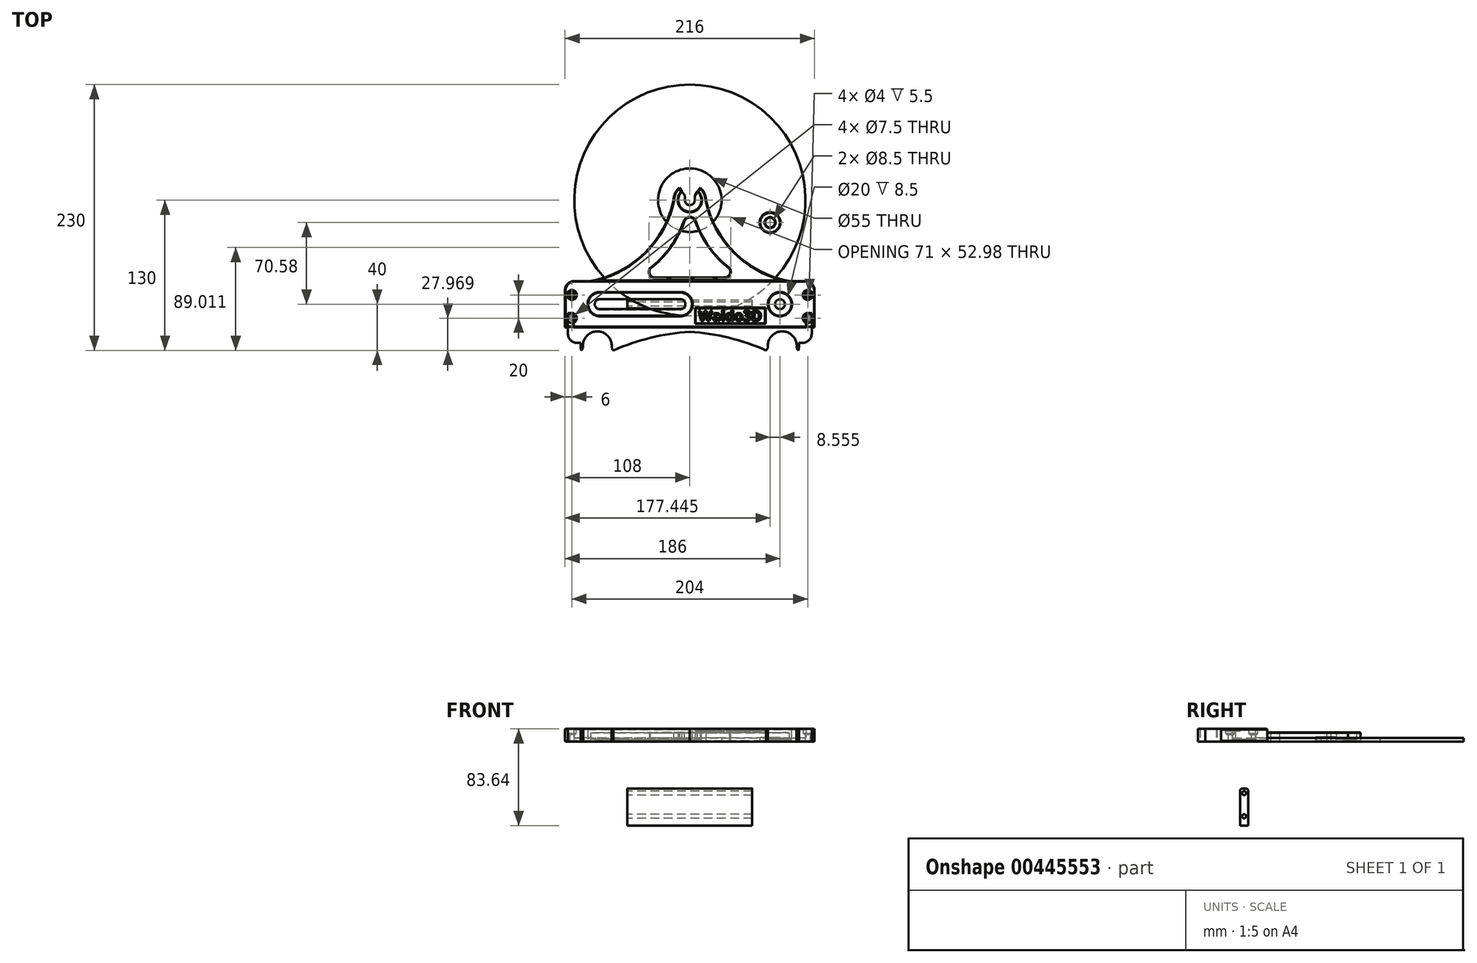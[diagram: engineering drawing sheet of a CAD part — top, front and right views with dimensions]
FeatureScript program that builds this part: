
annotation { "Feature Type Name" : "Feature", "Feature Type Description" : "" }
export const myFeature = defineFeature(function(context is Context, id is Id, definition is map)
    precondition{}
    {
        {
            var Q0;
            Q0=qCreatedBy(makeId("Top.planeOp"),FACE);
            var sketch = newSketch(context, id + "F0", { "sketchPlane" : qUnion([Q0])});
            skLineSegment(sketch, "E0", {"start": v(0, 0) * mm, "end": v(0, 90) * mm});
            skCircle(sketch, "E1", {"center": v(0, 90) * mm, "radius": 100 * mm});
            skCircle(sketch, "E2", {"center": v(0, 90) * mm, "radius": 27.5 * mm});
            skSolve(sketch);
        }
        {
            var Q0;
            Q0 = qSketchRegion(id + "F0", true);
            extrude(context, id + "F1", {"entities" : qUnion([Q0]), "depth" : 3 * mm});
        }
        {
            var Q0;
            Q0=qCreatedBy(makeId("Top.planeOp"),FACE);
            var sketch = newSketch(context, id + "F2", { "sketchPlane" : qUnion([Q0])});
            skLineSegment(sketch, "E3.top", {"start": v(100, 20.03) * mm, "end": v(-100, 20.03) * mm});
            skPoint(sketch, "E3.middle", {"position": v(0, 0) * mm});
            skArc(sketch, "E4", {"start": v(108, 12.03) * mm, "mid": v(105.66, 17.69) * mm, "end": v(100, 20.03) * mm});
            skPoint(sketch, "E5.orphan", {"position": v(108, 20.03) * mm});
            skArc(sketch, "E6.MirrorCS", {"start": v(-108, 12.03) * mm, "mid": v(-105.66, 17.69) * mm, "end": v(-100, 20.03) * mm});
            skPoint(sketch, "E7.orphan", {"position": v(-108, 20.03) * mm});
            skCircle(sketch, "E8", {"center": v(-78, 0) * mm, "radius": 4.25 * mm});
            skCircle(sketch, "E9", {"center": v(-8, 0) * mm, "radius": 4.25 * mm});
            skCircle(sketch, "E10", {"center": v(78, 0) * mm, "radius": 4.25 * mm});
            skLineSegment(sketch, "E11", {"start": v(-78, 4.25) * mm, "end": v(-8, 4.25) * mm});
            skLineSegment(sketch, "E12", {"start": v(-8.4, -4.23) * mm, "end": v(-77.6, -4.23) * mm});
            skPoint(sketch, "E13.orphan", {"position": v(108, -20.03) * mm});
            skPoint(sketch, "E14.orphan", {"position": v(-108, -20.03) * mm});
            skLineSegment(sketch, "E15", {"start": v(108, 12.03) * mm, "end": v(108, -20.03) * mm});
            skLineSegment(sketch, "E16", {"start": v(-108, -20.03) * mm, "end": v(-108, 12.03) * mm});
            skLineSegment(sketch, "E17", {"start": v(-108, -20.03) * mm, "end": v(108, -20.03) * mm});
            skCircle(sketch, "E18", {"center": v(102, 7.97) * mm, "radius": 2 * mm});
            skCircle(sketch, "E19", {"center": v(102, -12.03) * mm, "radius": 2 * mm});
            skCircle(sketch, "E20.MirrorC", {"center": v(-102, 7.97) * mm, "radius": 2 * mm});
            skCircle(sketch, "E21.MirrorC", {"center": v(-102, -12.03) * mm, "radius": 2 * mm});
            skSolve(sketch);
        }
        {
            var Q0;
            Q0 = qSketchRegion(id + "F2", true);
            extrude(context, id + "F3", {"entities" : qUnion([Q0]), "depth" : 11 * mm});
        }
        {
            var Q0;
            {var subQ0=sQuery(id+"F2.wireOp",EDGE,"E21.MirrorC");var subQ1=sQuery(id+"F2.wireOp",EDGE,"E20.MirrorC");var subQ2=sQuery(id+"F2.wireOp",EDGE,"E19");var subQ3=sQuery(id+"F2.wireOp",EDGE,"E18");var subQ4=sQuery(id+"F2.wireOp",EDGE,"E17");var subQ5=sQuery(id+"F2.wireOp",EDGE,"E6.MirrorCS");var subQ6=sQuery(id+"F2.wireOp",EDGE,"E4");var subQ7=sQuery(id+"F2.wireOp",EDGE,"E8");var subQ8=sQuery(id+"F2.wireOp",EDGE,"E3.top");var subQ9=sQuery(id+"F2.wireOp",EDGE,"E16");var subQ10=sQuery(id+"F2.wireOp",EDGE,"E9");var subQ11=sQuery(id+"F2.wireOp",EDGE,"E10");var subQ12=sQuery(id+"F2.wireOp",EDGE,"E11");var subQ13=sQuery(id+"F2.wireOp",EDGE,"E12");var subQ14=sQuery(id+"F2.wireOp",EDGE,"E15");Q0=makeQuery(id+"F7.boolean.opBoolean","SPLIT",FACE,{"disambiguationData":[TD([makeQuery(id+"F3.opExtrude","SWEPT_FACE",FACE,{"disambiguationData":[OSD([subQ8])]})])],"derivedFrom":makeQuery(id+"F3.opExtrude","CAP_FACE",FACE,{"disambiguationData":[OSD([subQ8,subQ6,subQ5,subQ7,subQ10,subQ11,subQ12,subQ13,subQ14,subQ9,subQ4,subQ3,subQ2,subQ1,subQ0])],"isStart":false})});}
            var sketch = newSketch(context, id + "F4", { "sketchPlane" : qUnion([Q0])});
            skLineSegment(sketch, "E22.bottom", {"start": v(65, -16.53) * mm, "end": v(5, -16.53) * mm});
            skLineSegment(sketch, "E22.top", {"start": v(65, -3.53) * mm, "end": v(5, -3.53) * mm});
            skLineSegment(sketch, "E22.left", {"start": v(65, -16.53) * mm, "end": v(65, -3.53) * mm});
            skLineSegment(sketch, "E22.right", {"start": v(5, -16.53) * mm, "end": v(5, -3.53) * mm});
            skPoint(sketch, "E22.middle", {"position": v(35, -10.03) * mm});
            skSolve(sketch);
        }
        {
            var Q0;
            Q0 = qSketchRegion(id + "F4", true);
            extrude(context, id + "F5", {"entities" : qUnion([Q0]), "operationType" : NewBodyOperationType.REMOVE, "oppositeDirection" : true, "depth" : 2 * mm});
        }
        {
            var Q0;
            Q0=makeQuery(id+"F5.boolean.opBoolean","COPY",FACE,{"derivedFrom":makeQuery(id+"F5.opExtrude","CAP_FACE",FACE,{"disambiguationData":[OSD([sQuery(id+"F4.wireOp",EDGE,"E22.bottom"),sQuery(id+"F4.wireOp",EDGE,"E22.top"),sQuery(id+"F4.wireOp",EDGE,"E22.left"),sQuery(id+"F4.wireOp",EDGE,"E22.right")])],"isStart":false})});
            var sketch = newSketch(context, id + "F6", { "sketchPlane" : qUnion([Q0])});
            skText(sketch, "E23", { "text": "Waldo3D", "fontName": "OpenSans-Bold.ttf"});
            skPoint(sketch, "E24.middle", {"position": v(35, -10.03) * mm});
            const initialGuessF6  = {"E23": [0.0075, -0.01448, 1, 0, 0.0089]};
            skSetInitialGuess(sketch, initialGuessF6);
            skSolve(sketch);
        }
        {
            var Q0;
            Q0 = qSketchRegion(id + "F6", true);
            extrude(context, id + "F7", {"entities" : qUnion([Q0]), "operationType" : NewBodyOperationType.ADD, "depth" : 2 * mm});
        }
        {
            var Q0;
            Q0=makeQuery(id+"F3.opExtrude","CAP_FACE",FACE,{"disambiguationData":[OSD([sQuery(id+"F2.wireOp",EDGE,"E3.bottom"),sQuery(id+"F2.wireOp",EDGE,"E3.top"),sQuery(id+"F2.wireOp",EDGE,"E3.left"),sQuery(id+"F2.wireOp",EDGE,"E3.right"),sQuery(id+"F2.wireOp",EDGE,"E4"),sQuery(id+"F2.wireOp",EDGE,"E6.MirrorCS"),sQuery(id+"F2.wireOp",EDGE,"E8"),sQuery(id+"F2.wireOp",EDGE,"E9"),sQuery(id+"F2.wireOp",EDGE,"E10"),sQuery(id+"F2.wireOp",EDGE,"E11"),sQuery(id+"F2.wireOp",EDGE,"E12")])],"isStart":false});
            var sketch = newSketch(context, id + "F8", { "sketchPlane" : qUnion([Q0])});
            skCircle(sketch, "E25", {"center": v(-78, 0) * mm, "radius": 10 * mm});
            skCircle(sketch, "E26", {"center": v(-8, 0) * mm, "radius": 10 * mm});
            skLineSegment(sketch, "E27", {"start": v(-78, 10) * mm, "end": v(-8, 10) * mm});
            skLineSegment(sketch, "E28", {"start": v(-8, -10) * mm, "end": v(-78, -10) * mm});
            skCircle(sketch, "E29", {"center": v(78, 0) * mm, "radius": 10 * mm});
            skSolve(sketch);
        }
        {
            var Q0;
            Q0 = qSketchRegion(id + "F8", true);
            extrude(context, id + "F9", {"entities" : qUnion([Q0]), "operationType" : NewBodyOperationType.REMOVE, "oppositeDirection" : true, "depth" : 9 * mm});
        }
        {
            var Q0;
            Q0=makeQuery(id+"F3.opExtrude","CAP_FACE",FACE,{"disambiguationData":[OSD([sQuery(id+"F2.wireOp",EDGE,"E3.bottom"),sQuery(id+"F2.wireOp",EDGE,"E3.top"),sQuery(id+"F2.wireOp",EDGE,"E3.left"),sQuery(id+"F2.wireOp",EDGE,"E3.right"),sQuery(id+"F2.wireOp",EDGE,"E4"),sQuery(id+"F2.wireOp",EDGE,"E6.MirrorCS"),sQuery(id+"F2.wireOp",EDGE,"E8"),sQuery(id+"F2.wireOp",EDGE,"E9"),sQuery(id+"F2.wireOp",EDGE,"E10"),sQuery(id+"F2.wireOp",EDGE,"E11"),sQuery(id+"F2.wireOp",EDGE,"E12")])],"isStart":false});
            var sketch = newSketch(context, id + "F10", { "sketchPlane" : qUnion([Q0])});
            skCircle(sketch, "E30", {"center": v(102, 7.97) * mm, "radius": 3.75 * mm});
            skCircle(sketch, "E31", {"center": v(102, -12.03) * mm, "radius": 3.75 * mm});
            skCircle(sketch, "E32.MirrorC", {"center": v(-102, 7.97) * mm, "radius": 3.75 * mm});
            skCircle(sketch, "E33.MirrorC", {"center": v(-102, -12.03) * mm, "radius": 3.75 * mm});
            skSolve(sketch);
        }
        {
            var Q0;
            Q0 = qSketchRegion(id + "F10", true);
            extrude(context, id + "F11", {"entities" : qUnion([Q0]), "operationType" : NewBodyOperationType.REMOVE, "oppositeDirection" : true, "depth" : 5 * mm});
        }
        {
            var Q0;
            Q0=makeQuery(id+"F11.boolean.opBoolean","COPY",EDGE,{"derivedFrom":makeQuery(id+"F11.opExtrude","CAP_EDGE",EDGE,{"disambiguationData":[OSD([sQuery(id+"F10.wireOp",EDGE,"E32.MirrorC")])],"isStart":false})});
            var Q1;
            Q1=makeQuery(id+"F11.boolean.opBoolean","COPY",EDGE,{"derivedFrom":makeQuery(id+"F11.opExtrude","CAP_EDGE",EDGE,{"disambiguationData":[OSD([sQuery(id+"F10.wireOp",EDGE,"E33.MirrorC")])],"isStart":false})});
            var Q2;
            Q2=makeQuery(id+"F11.boolean.opBoolean","COPY",EDGE,{"derivedFrom":makeQuery(id+"F11.opExtrude","CAP_EDGE",EDGE,{"disambiguationData":[OSD([sQuery(id+"F10.wireOp",EDGE,"E30")])],"isStart":false})});
            var Q3;
            Q3=makeQuery(id+"F11.boolean.opBoolean","COPY",EDGE,{"derivedFrom":makeQuery(id+"F11.opExtrude","CAP_EDGE",EDGE,{"disambiguationData":[OSD([sQuery(id+"F10.wireOp",EDGE,"E31")])],"isStart":false})});
            chamfer(context, id + "F12", {"entities" : qUnion([Q0, Q1, Q2, Q3]), "width" : 1 * mm, "tangentPropagation" : true});
        }
        {
            var Q0;
            Q0=qCreatedBy(makeId("Top.planeOp"),FACE);
            var sketch = newSketch(context, id + "F13", { "sketchPlane" : qUnion([Q0])});
            skLineSegment(sketch, "E34", {"start": v(0, 20) * mm, "end": v(86.03, 20) * mm});
            skLineSegment(sketch, "E35", {"start": v(0, 20) * mm, "end": v(0, 90) * mm});
            skArc(sketch, "E36", {"start": v(-8.97, 100.75) * mm, "mid": v(-12.68, 95.93) * mm, "end": v(-14, 90) * mm});
            skArc(sketch, "E37", {"start": v(-4.25, 90) * mm, "mid": v(0, 85.75) * mm, "end": v(4.25, 90) * mm});
            skLineSegment(sketch, "E38", {"start": v(4.25, 90) * mm, "end": v(4.25, 94) * mm});
            skLineSegment(sketch, "E39", {"start": v(4.25, 94) * mm, "end": v(8.97, 100.75) * mm});
            skLineSegment(sketch, "E40.MirrorCS", {"start": v(-4.25, 90) * mm, "end": v(-4.25, 94) * mm});
            skLineSegment(sketch, "E41.MirrorCS", {"start": v(-4.25, 94) * mm, "end": v(-8.97, 100.75) * mm});
            skArc(sketch, "E42", {"start": v(14, 90) * mm, "mid": v(39.34, 44.02) * mm, "end": v(86.03, 20) * mm});
            skArc(sketch, "E43.MirrorCS", {"start": v(-14, 90) * mm, "mid": v(-39.34, 44.02) * mm, "end": v(-86.03, 20) * mm});
            skLineSegment(sketch, "E44.MirrorCS", {"start": v(0, 20) * mm, "end": v(-86.03, 20) * mm});
            skArc(sketch, "E45", {"start": v(30, 23.02) * mm, "mid": v(34.34, 25.54) * mm, "end": v(34.32, 30.55) * mm});
            skArc(sketch, "E46.trimOffspring", {"start": v(14, 90) * mm, "mid": v(12.68, 95.93) * mm, "end": v(8.97, 100.75) * mm});
            skLineSegment(sketch, "E47", {"start": v(30, 23.02) * mm, "end": v(0, 23.02) * mm});
            skArc(sketch, "E48.MirrorC", {"start": v(-30, 23.02) * mm, "mid": v(-34.6, 26.06) * mm, "end": v(-33.61, 31.48) * mm});
            skLineSegment(sketch, "E49.MirrorCS", {"start": v(-30, 23.02) * mm, "end": v(0, 23.02) * mm});
            skCircle(sketch, "E50", {"center": v(0, 70) * mm, "radius": 5 * mm});
            skArc(sketch, "E51", {"start": v(4.77, 71.5) * mm, "mid": v(16.61, 48.9) * mm, "end": v(34.32, 30.55) * mm});
            skArc(sketch, "E52.MirrorCS", {"start": v(-4.77, 71.5) * mm, "mid": v(-16.61, 48.9) * mm, "end": v(-34.32, 30.55) * mm});
            skSolve(sketch);
        }
        {
            var Q0;
            Q0 = qSketchRegion(id + "F13", true);
            extrude(context, id + "F14", {"entities" : qUnion([Q0]), "depth" : 8 * mm});
        }
        {
            var Q0;
            Q0=makeQuery(id+"F14.opExtrude","CAP_FACE",FACE,{"disambiguationData":[OSD([sQuery(id+"F13.wireOp",EDGE,"E34"),sQuery(id+"F13.wireOp",EDGE,"E36"),sQuery(id+"F13.wireOp",EDGE,"E37"),sQuery(id+"F13.wireOp",EDGE,"E38"),sQuery(id+"F13.wireOp",EDGE,"E39"),sQuery(id+"F13.wireOp",EDGE,"E40.MirrorCS"),sQuery(id+"F13.wireOp",EDGE,"E41.MirrorCS"),sQuery(id+"F13.wireOp",EDGE,"E42"),sQuery(id+"F13.wireOp",EDGE,"E43.MirrorCS"),sQuery(id+"F13.wireOp",EDGE,"E44.MirrorCS"),sQuery(id+"F13.wireOp",EDGE,"klo4OWiA-xBeZ-rQVl-mnmB-Yb4P8nKjesbg"),sQuery(id+"F13.wireOp",EDGE,"E45"),sQuery(id+"F13.wireOp",EDGE,"E46.trimOffspring"),sQuery(id+"F13.wireOp",EDGE,"pojwg80n-vTzl-4vHL-MMqQ-xkOF31NqBd4l"),sQuery(id+"F13.wireOp",EDGE,"E47"),sQuery(id+"F13.wireOp",EDGE,"45ded926-9557-4482-96ae-ffeaec27a78e0.MirrorCS"),sQuery(id+"F13.wireOp",EDGE,"E48.MirrorC"),sQuery(id+"F13.wireOp",EDGE,"E49.MirrorCS")])],"isStart":false});
            var sketch = newSketch(context, id + "F15", { "sketchPlane" : qUnion([Q0])});
            skCircle(sketch, "E53", {"center": v(0, 90) * mm, "radius": 10 * mm});
            skSolve(sketch);
        }
        {
            var Q0;
            Q0 = qSketchRegion(id + "F15", true);
            extrude(context, id + "F16", {"entities" : qUnion([Q0]), "operationType" : NewBodyOperationType.REMOVE, "oppositeDirection" : true, "depth" : 6 * mm});
        }
        {
            var Q0;
            Q0=makeQuery(id+"F3.opExtrude","CAP_FACE",FACE,{"disambiguationData":[OSD([sQuery(id+"F2.wireOp",EDGE,"E3.top"),sQuery(id+"F2.wireOp",EDGE,"E4"),sQuery(id+"F2.wireOp",EDGE,"E6.MirrorCS"),sQuery(id+"F2.wireOp",EDGE,"E8"),sQuery(id+"F2.wireOp",EDGE,"E9"),sQuery(id+"F2.wireOp",EDGE,"E10"),sQuery(id+"F2.wireOp",EDGE,"E11"),sQuery(id+"F2.wireOp",EDGE,"E12"),sQuery(id+"F2.wireOp",EDGE,"E15"),sQuery(id+"F2.wireOp",EDGE,"E16"),sQuery(id+"F2.wireOp",EDGE,"E17"),sQuery(id+"F2.wireOp",EDGE,"E18"),sQuery(id+"F2.wireOp",EDGE,"E19"),sQuery(id+"F2.wireOp",EDGE,"E20.MirrorC"),sQuery(id+"F2.wireOp",EDGE,"E21.MirrorC")])],"isStart":false});
            var Q1;
            Q1=makeQuery(id+"F14.opExtrude","CAP_FACE",FACE,{"disambiguationData":[OSD([sQuery(id+"F13.wireOp",EDGE,"E34"),sQuery(id+"F13.wireOp",EDGE,"E36"),sQuery(id+"F13.wireOp",EDGE,"E37"),sQuery(id+"F13.wireOp",EDGE,"E38"),sQuery(id+"F13.wireOp",EDGE,"E39"),sQuery(id+"F13.wireOp",EDGE,"E40.MirrorCS"),sQuery(id+"F13.wireOp",EDGE,"E41.MirrorCS"),sQuery(id+"F13.wireOp",EDGE,"E42"),sQuery(id+"F13.wireOp",EDGE,"E43.MirrorCS"),sQuery(id+"F13.wireOp",EDGE,"E44.MirrorCS"),sQuery(id+"F13.wireOp",EDGE,"E45"),sQuery(id+"F13.wireOp",EDGE,"E46.trimOffspring"),sQuery(id+"F13.wireOp",EDGE,"E47"),sQuery(id+"F13.wireOp",EDGE,"E48.MirrorC"),sQuery(id+"F13.wireOp",EDGE,"E49.MirrorCS"),sQuery(id+"F13.wireOp",EDGE,"E50"),sQuery(id+"F13.wireOp",EDGE,"E51"),sQuery(id+"F13.wireOp",EDGE,"E52.MirrorCS")])],"isStart":false});
            var Q2;
            Q2=makeQuery(id+"F21.opBoolean","MERGE",FACE,{"derivedFrom":[makeQuery(id+"F3.opExtrude","CAP_FACE",FACE,{"disambiguationData":[OSD([sQuery(id+"F2.wireOp",EDGE,"E3.top"),sQuery(id+"F2.wireOp",EDGE,"E4"),sQuery(id+"F2.wireOp",EDGE,"E6.MirrorCS"),sQuery(id+"F2.wireOp",EDGE,"E8"),sQuery(id+"F2.wireOp",EDGE,"E9"),sQuery(id+"F2.wireOp",EDGE,"E10"),sQuery(id+"F2.wireOp",EDGE,"E11"),sQuery(id+"F2.wireOp",EDGE,"E12"),sQuery(id+"F2.wireOp",EDGE,"E15"),sQuery(id+"F2.wireOp",EDGE,"E16"),sQuery(id+"F2.wireOp",EDGE,"E17"),sQuery(id+"F2.wireOp",EDGE,"E18"),sQuery(id+"F2.wireOp",EDGE,"E19"),sQuery(id+"F2.wireOp",EDGE,"E20.MirrorC"),sQuery(id+"F2.wireOp",EDGE,"E21.MirrorC")])],"isStart":true}),makeQuery(id+"F14.opExtrude","CAP_FACE",FACE,{"disambiguationData":[OSD([sQuery(id+"F13.wireOp",EDGE,"E34"),sQuery(id+"F13.wireOp",EDGE,"E36"),sQuery(id+"F13.wireOp",EDGE,"E37"),sQuery(id+"F13.wireOp",EDGE,"E38"),sQuery(id+"F13.wireOp",EDGE,"E39"),sQuery(id+"F13.wireOp",EDGE,"E40.MirrorCS"),sQuery(id+"F13.wireOp",EDGE,"E41.MirrorCS"),sQuery(id+"F13.wireOp",EDGE,"E42"),sQuery(id+"F13.wireOp",EDGE,"E43.MirrorCS"),sQuery(id+"F13.wireOp",EDGE,"E44.MirrorCS"),sQuery(id+"F13.wireOp",EDGE,"E45"),sQuery(id+"F13.wireOp",EDGE,"E46.trimOffspring"),sQuery(id+"F13.wireOp",EDGE,"E47"),sQuery(id+"F13.wireOp",EDGE,"E48.MirrorC"),sQuery(id+"F13.wireOp",EDGE,"E49.MirrorCS"),sQuery(id+"F13.wireOp",EDGE,"E50"),sQuery(id+"F13.wireOp",EDGE,"E51"),sQuery(id+"F13.wireOp",EDGE,"E52.MirrorCS")])],"isStart":true})]});
            chamfer(context, id + "F17", {"entities" : qUnion([Q0, Q1, Q2]), "width" : .5 * mm, "tangentPropagation" : true});
        }
        {
            var Q0;
            Q0=qCreatedBy(makeId("Right.planeOp"),FACE);
            var sketch = newSketch(context, id + "F18", { "sketchPlane" : qUnion([Q0])});
            skLineSegment(sketch, "E54.bottom", {"start": v(3.5, -72.64) * mm, "end": v(-3.5, -72.64) * mm});
            skLineSegment(sketch, "E54.top", {"start": v(3.5, -40.64) * mm, "end": v(-3.5, -40.64) * mm});
            skLineSegment(sketch, "E54.left", {"start": v(3.5, -72.64) * mm, "end": v(3.5, -40.64) * mm});
            skLineSegment(sketch, "E54.right", {"start": v(-3.5, -72.64) * mm, "end": v(-3.5, -40.64) * mm});
            skPoint(sketch, "E54.middle", {"position": v(0, -56.64) * mm});
            skCircle(sketch, "E55", {"center": v(0, -64.64) * mm, "radius": 1.75 * mm});
            skCircle(sketch, "E56", {"center": v(0, -44.64) * mm, "radius": 1.75 * mm});
            skSolve(sketch);
        }
        {
            var Q0;
            Q0 = qSketchRegion(id + "F18", true);
            extrude(context, id + "F19", {"entities" : qUnion([Q0]), "depth" : 108 * mm, "symmetric" : true});
        }
        {
            var Q0;
            Q0=makeQuery(id+"F19.opExtrude","SWEPT_EDGE",EDGE,{"disambiguationData":[OSD([sQuery(id+"F18.wireOp",EDGE,"E54.top"),sQuery(id+"F18.wireOp",EDGE,"E54.right")])]});
            var Q1;
            Q1=makeQuery(id+"F19.opExtrude","SWEPT_EDGE",EDGE,{"disambiguationData":[OSD([sQuery(id+"F18.wireOp",EDGE,"E54.top"),sQuery(id+"F18.wireOp",EDGE,"E54.left")])]});
            fillet(context, id + "F20", {"entities" : qUnion([Q0, Q1]), "radius" : 2 * mm, "tangentPropagation" : true, "allowEdgeOverflow" : false});
        }
        {
            var Q0;
            Q0=makeQuery(id+"F3.opExtrude","SWEPT_BODY",BODY,{"disambiguationData":[OSD([sQuery(id+"F2.wireOp",EDGE,"E3.top"),sQuery(id+"F2.wireOp",EDGE,"E4"),sQuery(id+"F2.wireOp",EDGE,"E6.MirrorCS"),sQuery(id+"F2.wireOp",EDGE,"E8"),sQuery(id+"F2.wireOp",EDGE,"E9"),sQuery(id+"F2.wireOp",EDGE,"E10"),sQuery(id+"F2.wireOp",EDGE,"E11"),sQuery(id+"F2.wireOp",EDGE,"E12"),sQuery(id+"F2.wireOp",EDGE,"E15"),sQuery(id+"F2.wireOp",EDGE,"E16"),sQuery(id+"F2.wireOp",EDGE,"E17")])]});
            var Q1;
            Q1=makeQuery(id+"F14.opExtrude","SWEPT_BODY",BODY,{"disambiguationData":[OSD([sQuery(id+"F13.wireOp",EDGE,"E34"),sQuery(id+"F13.wireOp",EDGE,"E36"),sQuery(id+"F13.wireOp",EDGE,"E37"),sQuery(id+"F13.wireOp",EDGE,"E38"),sQuery(id+"F13.wireOp",EDGE,"E39"),sQuery(id+"F13.wireOp",EDGE,"E40.MirrorCS"),sQuery(id+"F13.wireOp",EDGE,"E41.MirrorCS"),sQuery(id+"F13.wireOp",EDGE,"E42"),sQuery(id+"F13.wireOp",EDGE,"E43.MirrorCS"),sQuery(id+"F13.wireOp",EDGE,"E44.MirrorCS"),sQuery(id+"F13.wireOp",EDGE,"E45"),sQuery(id+"F13.wireOp",EDGE,"E46.trimOffspring"),sQuery(id+"F13.wireOp",EDGE,"E47"),sQuery(id+"F13.wireOp",EDGE,"E48.MirrorC"),sQuery(id+"F13.wireOp",EDGE,"E49.MirrorCS"),sQuery(id+"F13.wireOp",EDGE,"E50"),sQuery(id+"F13.wireOp",EDGE,"E51"),sQuery(id+"F13.wireOp",EDGE,"E52.MirrorCS")])]});
            booleanBodies(context, id + "F21", {"operationType" : BooleanOperationType.UNION, "tools" : qUnion([Q0, Q1])});
        }
        {
            var Q0;
            Q0=qCreatedBy(makeId("Top.planeOp"),FACE);
            var sketch = newSketch(context, id + "F22", { "sketchPlane" : qUnion([Q0])});
            skCircle(sketch, "E57", {"center": v(69.44, 70.58) * mm, "radius": 4.25 * mm});
            skCircle(sketch, "E58", {"center": v(69.44, 70.58) * mm, "radius": 9 * mm});
            skSolve(sketch);
        }
        {
            var Q0;
            Q0 = qSketchRegion(id + "F22", true);
            extrude(context, id + "F23", {"entities" : qUnion([Q0]), "depth" : 3.5 * mm});
        }
        {
            var Q0;
            Q0=makeQuery(id+"F23.opExtrude","CAP_FACE",FACE,{"disambiguationData":[OSD([sQuery(id+"F22.wireOp",EDGE,"E57"),sQuery(id+"F22.wireOp",EDGE,"E58")])],"isStart":false});
            var Q1;
            Q1=makeQuery(id+"F23.opExtrude","CAP_EDGE",EDGE,{"disambiguationData":[OSD([sQuery(id+"F22.wireOp",EDGE,"E58")])],"isStart":true});
            var Q2;
            Q2=makeQuery(id+"F23.opExtrude","CAP_EDGE",EDGE,{"disambiguationData":[OSD([sQuery(id+"F22.wireOp",EDGE,"E57")])],"isStart":true});
            chamfer(context, id + "F24", {"entities" : qUnion([Q0, Q1, Q2]), "width" : .5 * mm, "tangentPropagation" : true});
        }
        {
            var Q0;
            Q0=qCreatedBy(makeId("Top.planeOp"),FACE);
            var sketch = newSketch(context, id + "F25", { "sketchPlane" : qUnion([Q0])});
            skArc(sketch, "E59", {"start": v(92.34, -38) * mm, "mid": v(80, -23.5) * mm, "end": v(67.66, -38) * mm});
            skArc(sketch, "E60", {"start": v(93.94, -40) * mm, "mid": v(80, -21.5) * mm, "end": v(66.06, -40) * mm});
            skLineSegment(sketch, "E61", {"start": v(0, -20) * mm, "end": v(100.5, -20) * mm});
            skLineSegment(sketch, "E62", {"start": v(100.5, -20) * mm, "end": v(100.5, -7.57) * mm});
            skLineSegment(sketch, "E63", {"start": v(100.5, -7.57) * mm, "end": v(105.5, -7.57) * mm});
            skLineSegment(sketch, "E64", {"start": v(105.5, -7.57) * mm, "end": v(105.5, -25.51) * mm});
            skLineSegment(sketch, "E65", {"start": v(80, -36) * mm, "end": v(80, -38) * mm});
            skLineSegment(sketch, "E66", {"start": v(93.94, -40) * mm, "end": v(92.34, -38) * mm});
            skLineSegment(sketch, "E67", {"start": v(66.06, -40) * mm, "end": v(67.66, -38) * mm});
            skLineSegment(sketch, "E68.bottom", {"start": v(5, -20) * mm, "end": v(57.48, -20) * mm});
            skArc(sketch, "E69", {"start": v(66.06, -40) * mm, "mid": v(33.74, -29.07) * mm, "end": v(0, -24) * mm});
            skLineSegment(sketch, "E70", {"start": v(94.28, -33.51) * mm, "end": v(97.5, -33.51) * mm});
            skPoint(sketch, "E71.start.orphan", {"position": v(105.5, -40) * mm});
            skArc(sketch, "E72", {"start": v(97.5, -33.51) * mm, "mid": v(103.16, -31.17) * mm, "end": v(105.5, -25.51) * mm});
            skPoint(sketch, "E73.orphan", {"position": v(105.5, -33.51) * mm});
            skLineSegment(sketch, "E74.MirrorCS", {"start": v(-93.94, -40) * mm, "end": v(-92.34, -38) * mm});
            skLineSegment(sketch, "E75.MirrorCS", {"start": v(-66.06, -40) * mm, "end": v(-67.66, -38) * mm});
            skLineSegment(sketch, "E76.MirrorCS", {"start": v(-80, -36) * mm, "end": v(-80, -38) * mm});
            skArc(sketch, "E77.MirrorCS", {"start": v(-92.34, -38) * mm, "mid": v(-80, -23.5) * mm, "end": v(-67.66, -38) * mm});
            skLineSegment(sketch, "E78.MirrorCS", {"start": v(0, -20) * mm, "end": v(-100.5, -20) * mm});
            skLineSegment(sketch, "E79.MirrorCS", {"start": v(-100.5, -20) * mm, "end": v(-100.5, -7.57) * mm});
            skLineSegment(sketch, "E80.MirrorCS", {"start": v(-105.5, -7.57) * mm, "end": v(-105.5, -25.51) * mm});
            skLineSegment(sketch, "E81.MirrorCS", {"start": v(-100.5, -7.57) * mm, "end": v(-105.5, -7.57) * mm});
            skPoint(sketch, "E82.MirrorP", {"position": v(-105.5, -33.51) * mm});
            skLineSegment(sketch, "E83.MirrorCS", {"start": v(-94.28, -33.51) * mm, "end": v(-97.5, -33.51) * mm});
            skLineSegment(sketch, "E84.MirrorCS", {"start": v(-5, -20) * mm, "end": v(-57.48, -20) * mm});
            skArc(sketch, "E85.MirrorCS", {"start": v(-93.94, -40) * mm, "mid": v(-80, -21.5) * mm, "end": v(-66.06, -40) * mm});
            skPoint(sketch, "E86.MirrorP", {"position": v(-105.5, -40) * mm});
            skArc(sketch, "E87.MirrorCS", {"start": v(-97.5, -33.51) * mm, "mid": v(-103.16, -31.17) * mm, "end": v(-105.5, -25.51) * mm});
            skArc(sketch, "E88.MirrorCS", {"start": v(-66.06, -40) * mm, "mid": v(-33.74, -29.07) * mm, "end": v(0, -24) * mm});
            skSolve(sketch);
        }
        {
            var Q0;
            Q0 = qSketchRegion(id + "F25", true);
            extrude(context, id + "F26", {"entities" : qUnion([Q0]), "depth" : 11 * mm});
        }
    });
